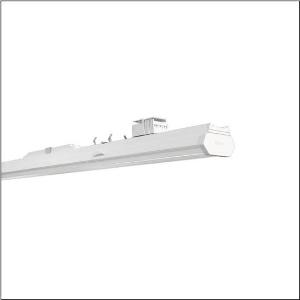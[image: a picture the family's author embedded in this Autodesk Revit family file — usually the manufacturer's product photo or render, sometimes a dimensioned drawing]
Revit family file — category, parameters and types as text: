
# Revit family: licross_r__11_protected_ho_51tp11mn4gxs_ec8e
name_source: partatom
category: Lighting Fixtures
units: mm (PartAtom-declared; Revit-internal decimal feet)

## family parameters
Cut with Voids When Loaded = No
Host = Face
Light Source = No
Part Type = Normal
Room Calculation Point = No
Round Connector Dimension = Use Diameter
Shared = No

## types (1)
- --- (1 x LED, 16070 lm, 87.4 W, 4000K)
    Apparent Load = 87 VA
    CIE Flux Codes = 84 94 98 99 100
    Color Rendering = 80
    Color Temperature = 4000K
    Default Elevation = 1800 mm
    Description = Licross® 11 Protected HO, luminaire insert, of sheet steel, galvanised, coil coated, white, length: 1.500mm, width: 90mm, height: 101mm, LED rated luminous flux: 16.070lm, light colour: 840, control gear: ON/OFF Multilumen, with plug, 3-pole, with phase selection, mains connection: 220..240V, AC, 50/60Hz, rated input power: 87W, halogen-free wiring, primary light control with lens, of plastic, primary optical cover: cover, of PMMA, light emission: direct distribution, primary light characteristic: symmetric, protection rating (complete): IP64, insulation class (complete): insulation class I (protective earthing), certification: CE, ENEC, VDE, UKCA, protection symbol: D if used in an environment with conductive dust loads with corresponding accessories, impact resistance: IK06, permissible ambient temperature for indoor applications: -35..+35°C, corresponds to IFS (International Featured Standards) requirements for safety and quality in the food industry, reducing of maximum allowable ambient temperature of 5°C with ceiling mounting, LABS conformity tested according to VDMA 24364:2018-05, packaging unit: 1 piece
    Height = 92 mm
    Lamp = 1 x LED
    Lamp Light Flux = 16070 lm
    Lamp Power = 87.4 W
    Lamp count = 1
    Length = 1500 mm
    Luminous efficacy = 184 lm/W
    Manufacturer = Siteco
    ModVariant = No
    Model = 51TP11MN4GXS
    Mounting Place = Ceiling
    Mounting Type = Pendant
    Number of Poles = 1
    OnlyDefault = Yes
    Power Factor = 1
    Product Name = Licross® 11 Protected HO
    Product group = luminaire insert
    ProductGroupID = 901
    Protection Class = Protection class I
    Protection Degree = IP 64
    RLX_Detail_Level = 1
    RLX_Emergency_Light_Flux = 0 lm
    RLX_Emergency_Type = 0
    RLX_Emergency_Type_DB = No
    RlxData = <blob elided: 21949 chars, md5=3bf712e9>
    Socket = socket
    Standby Power = 0 W
    System Light Flux = 16070 lm
    System Power = 87 W
    Type Comments = factory setting: luminous flux: 100 % | (A | C | E) | 203 mA
    Type Image = l_1256148.jpg
    URL = http://relux.com
    VarID = @adj_019363
    Voltage = 0 V
    Weight = 0.00 kg
    Width = 88 mm

## geometry (parser evidence)
native form markers: Blend x4, Sweep x11
no freeform markers — native parametric forms only
